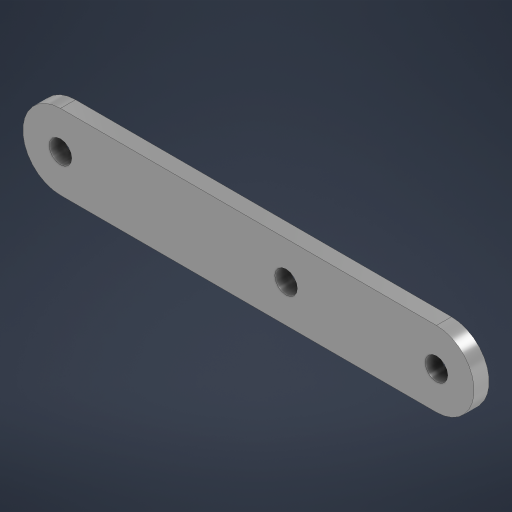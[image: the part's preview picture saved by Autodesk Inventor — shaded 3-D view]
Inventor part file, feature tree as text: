
AUTODESK INVENTOR PART (.ipt)
format: ipt  version: 2023 (Build 270158000, 158)  size: 191,488 bytes
history: native  units: mm
features: extrude x2, sketch x2, fillet x1
ambient origin geometry x8: Origin, YZ Plane, XZ Plane, XY Plane, X Axis, Y Axis, Z Axis, Center Point
bodies: Solid1 (feature_tree)
feature tree (5):
  extrude  "Extrusion1"  Depth=10.0mm
  fillet  "Fillet1"  Radius=2.0mm
  extrude  "Extrusion2"  Depth=5.0mm
  sketch  "Sketch1"  dims[d0=60.0mm d1=10.0mm d2=2.0mm d3=0.0mm]
  sketch  "Sketch2"  dims[d4=5.0mm d5=3.0mm d6=3.0mm d7=2.0mm d8=0.0mm d9=5.0mm d10=3.0mm]
